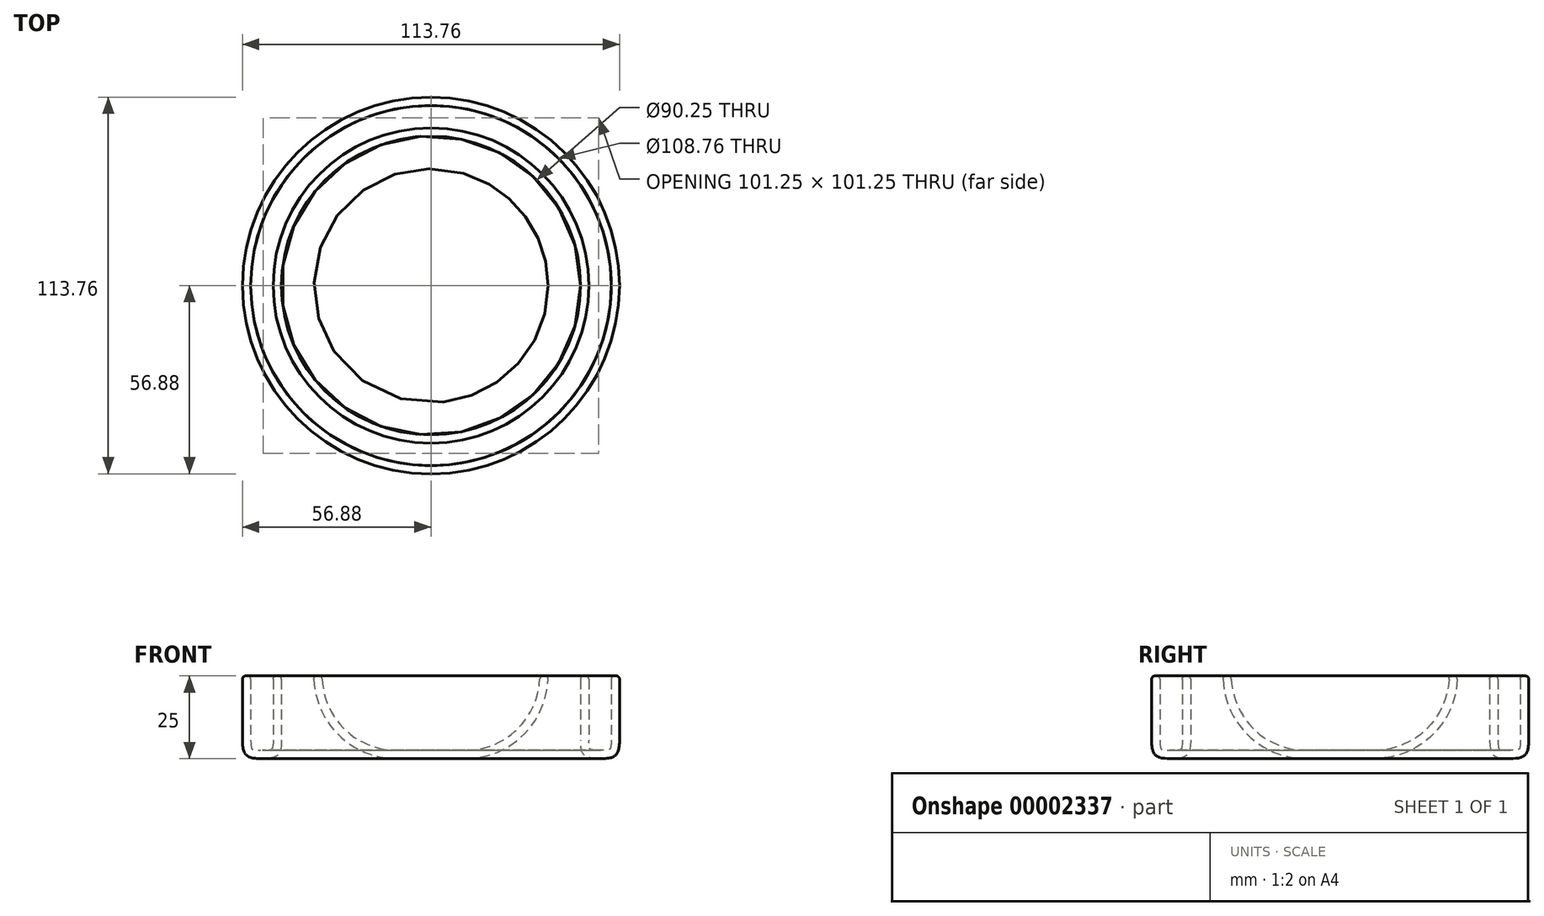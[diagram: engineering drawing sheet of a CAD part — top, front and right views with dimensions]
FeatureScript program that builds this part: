
annotation { "Feature Type Name" : "Feature", "Feature Type Description" : "" }
export const myFeature = defineFeature(function(context is Context, id is Id, definition is map)
    precondition{}
    {
        {
            var Q0;
            Q0=qCreatedBy(makeId("Top.planeOp"),FACE);
            var sketch = newSketch(context, id + "F0", { "sketchPlane" : qUnion([Q0])});
            skCircle(sketch, "E0", {"center": v(0, 0) * mm, "radius": 45.12 * mm});
            skCircle(sketch, "E1", {"center": v(0, 0) * mm, "radius": 35.36 * mm});
            skCircle(sketch, "E2", {"center": v(0, 0) * mm, "radius": 56.88 * mm});
            skSolve(sketch);
        }
        {
            var Q0;
            Q0 = qSketchRegion(id + "F0", true);
            var Q1;
            Q1=makeQuery(id+"F0.imprint","IMPRINT",FACE,{"disambiguationData":[TD([[makeQuery(id+"F0.imprint","IMPRINT",EDGE,{"derivedFrom":sQuery(id+"F0.wireOp",EDGE,"E1")}),1.0]])]});
            extrude(context, id + "F1", {"entities" : qUnion([Q0, Q1]), "depth" : 25 * mm});
        }
        {
            var Q0;
            Q0=makeQuery(id+"F1.opExtrude","CAP_FACE",FACE,{"disambiguationData":[OSD([sQuery(id+"F0.wireOp",EDGE,"E0"),sQuery(id+"F0.wireOp",EDGE,"E2")])],"isStart":true});
            fillet(context, id + "F2", {"entities" : qUnion([Q0]), "radius" : 5.5 * mm, "tangentPropagation" : true, "rho" : 0.6, "crossSection" : FilletCrossSection.CONIC, "allowEdgeOverflow" : false});
        }
        {
            var Q0;
            Q0=makeQuery(id+"F1.opExtrude","CAP_FACE",FACE,{"disambiguationData":[OSD([sQuery(id+"F0.wireOp",EDGE,"E0"),sQuery(id+"F0.wireOp",EDGE,"E2")])],"isStart":false});
            shell(context, id + "F3", {"entities" : qUnion([Q0]), "thickness" : 2.5 * mm});
        }
        {
            var Q0;
            Q0=makeQuery(id+"F1.opExtrude","CAP_FACE",FACE,{"disambiguationData":[OSD([sQuery(id+"F0.wireOp",EDGE,"E0"),sQuery(id+"F0.wireOp",EDGE,"E2")])],"isStart":false});
            var Q1;
            {var subQ0=sQuery(id+"F0.wireOp",EDGE,"E0");var subQ1=sQuery(id+"F0.wireOp",EDGE,"E2");Q1=makeQuery(id+"F3.opShell","OFFSET_FACE",FACE,{"disambiguationData":[OSD([subQ0,subQ1]),TDD([makeQuery(id+"F1.opExtrude","CAP_FACE",FACE,{"disambiguationData":[OSD([subQ0,subQ1])],"isStart":false})])]});}
            fillet(context, id + "F4", {"entities" : qUnion([Q0, Q1]), "radius" : 1 * mm, "tangentPropagation" : true, "allowEdgeOverflow" : false});
        }
        {
            var Q0;
            Q0=makeQuery(id+"F1.opExtrude","CAP_FACE",FACE,{"disambiguationData":[OSD([sQuery(id+"F0.wireOp",EDGE,"E1")])],"isStart":true});
            fillet(context, id + "F5", {"entities" : qUnion([Q0]), "radius" : 25 * mm, "tangentPropagation" : true, "allowEdgeOverflow" : false});
        }
        {
            var Q0;
            Q0=makeQuery(id+"F1.opExtrude","CAP_FACE",FACE,{"disambiguationData":[OSD([sQuery(id+"F0.wireOp",EDGE,"E1")])],"isStart":false});
            shell(context, id + "F6", {"entities" : qUnion([Q0]), "thickness" : 2.5 * mm});
        }
        {
            var Q0;
            Q0=makeQuery(id+"F1.opExtrude","CAP_FACE",FACE,{"disambiguationData":[OSD([sQuery(id+"F0.wireOp",EDGE,"E1")])],"isStart":false});
            fillet(context, id + "F7", {"entities" : qUnion([Q0]), "radius" : 1 * mm, "tangentPropagation" : true, "allowEdgeOverflow" : false});
        }
    });
